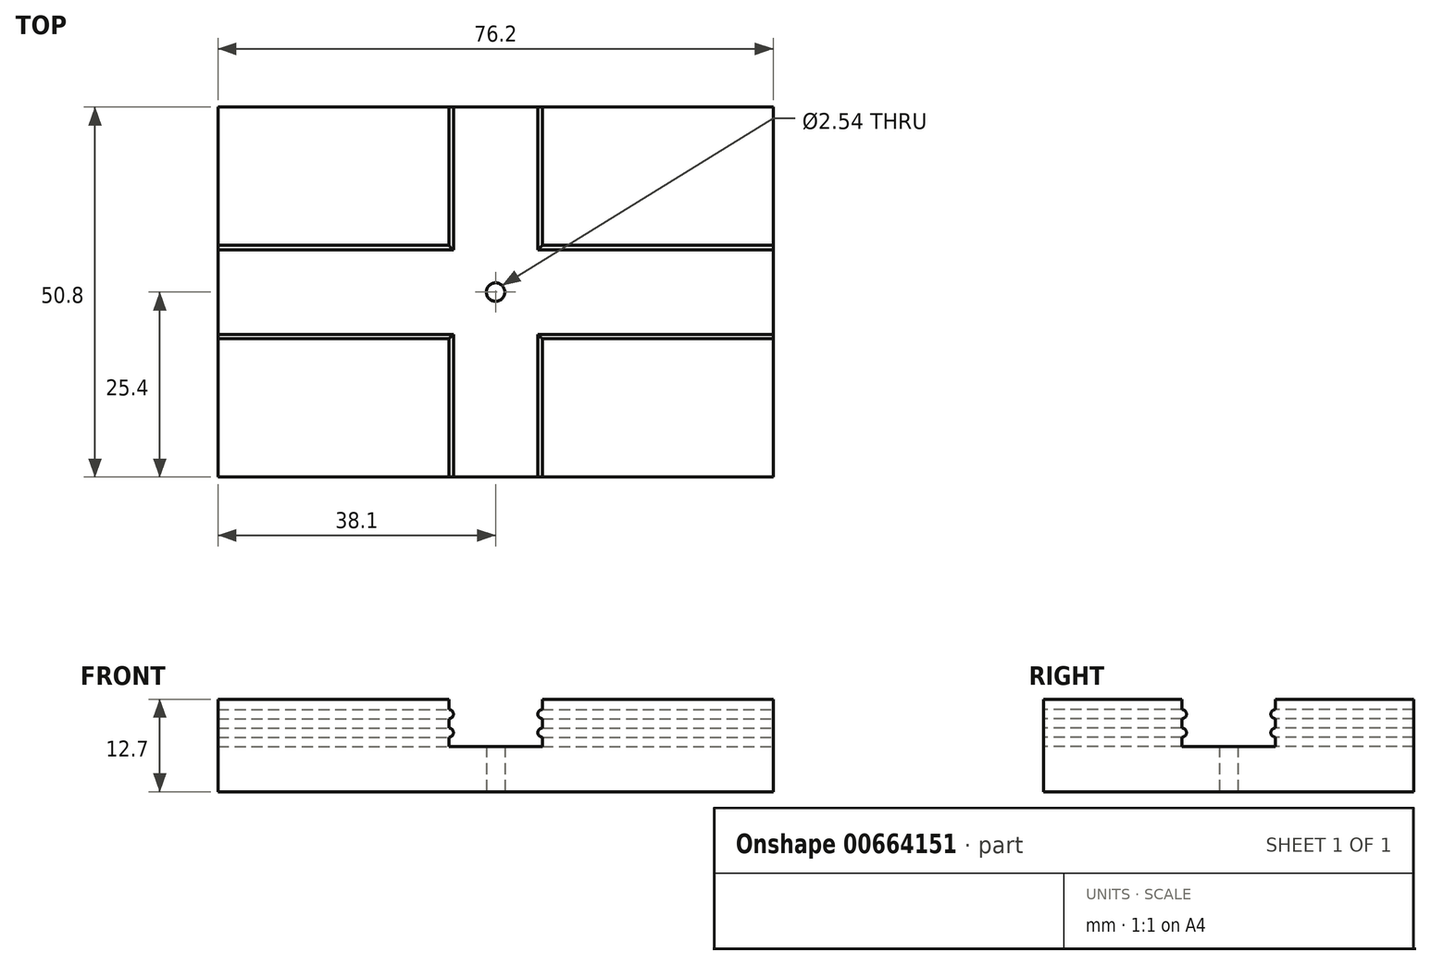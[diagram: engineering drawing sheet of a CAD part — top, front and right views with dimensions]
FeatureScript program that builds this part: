
annotation { "Feature Type Name" : "Feature", "Feature Type Description" : "" }
export const myFeature = defineFeature(function(context is Context, id is Id, definition is map)
    precondition{}
    {
        {
            var Q0;
            Q0=qCreatedBy(makeId("Top.planeOp"),FACE);
            var sketch = newSketch(context, id + "F0", { "sketchPlane" : qUnion([Q0])});
            skLineSegment(sketch, "E0.bottom", {"start": v(-38.1, -25.4) * mm, "end": v(38.1, -25.4) * mm});
            skLineSegment(sketch, "E0.top", {"start": v(-38.1, 25.4) * mm, "end": v(38.1, 25.4) * mm});
            skLineSegment(sketch, "E0.left", {"start": v(-38.1, -25.4) * mm, "end": v(-38.1, 25.4) * mm});
            skLineSegment(sketch, "E0.right", {"start": v(38.1, -25.4) * mm, "end": v(38.1, 25.4) * mm});
            skPoint(sketch, "E0.middle", {"position": v(0, 0) * mm});
            skSolve(sketch);
        }
        {
            var Q0;
            Q0=makeQuery(id+"F0.imprint","IMPRINT",FACE,{"disambiguationData":[TD([[makeQuery(id+"F0.imprint","IMPRINT",EDGE,{"derivedFrom":sQuery(id+"F0.wireOp",EDGE,"E0.bottom")}),1.0]])]});
            extrude(context, id + "F1", {"entities" : qUnion([Q0]), "depth" : 12.7 * mm, "offsetDistance" : 25.4 * mm});
        }
        {
            var Q0;
            Q0=makeQuery(id+"F1.opExtrude","SWEPT_FACE",FACE,{"disambiguationData":[OSD([sQuery(id+"F0.wireOp",EDGE,"E0.bottom")])]});
            var sketch = newSketch(context, id + "F2", { "sketchPlane" : qUnion([Q0])});
            skLineSegment(sketch, "E1.bottom", {"start": v(-6.41, 12.7) * mm, "end": v(6.41, 12.7) * mm});
            skLineSegment(sketch, "E1.top", {"start": v(-6.41, 6.22) * mm, "end": v(6.41, 6.22) * mm});
            skLineSegment(sketch, "E1.left", {"start": v(-6.41, 12.7) * mm, "end": v(-6.41, 6.22) * mm});
            skLineSegment(sketch, "E1.right", {"start": v(6.41, 12.7) * mm, "end": v(6.41, 6.22) * mm});
            skArc(sketch, "E2", {"start": v(-6.41, 11.28) * mm, "mid": v(-5.8, 10.66) * mm, "end": v(-6.41, 10.03) * mm});
            skArc(sketch, "E3", {"start": v(-6.41, 8.74) * mm, "mid": v(-5.8, 8.12) * mm, "end": v(-6.41, 7.5) * mm});
            skArc(sketch, "E4.MirrorCS", {"start": v(6.41, 11.28) * mm, "mid": v(5.8, 10.66) * mm, "end": v(6.41, 10.03) * mm});
            skArc(sketch, "E5.MirrorCS", {"start": v(6.41, 8.74) * mm, "mid": v(5.8, 8.12) * mm, "end": v(6.41, 7.5) * mm});
            skSolve(sketch);
        }
        {
            var Q0;
            {var subQ3=sQuery(id+"F2.wireOp",EDGE,"E1.bottom");Q0=makeQuery(id+"F2.imprint","IMPRINT",FACE,{"disambiguationData":[TD([[makeQuery(id+"F2.imprint","IMPRINT",EDGE,{"derivedFrom":subQ3}),-1.0]])]});}
            var Q1;
            Q1 = qSketchRegion(id + "F4", true);
            extrude(context, id + "F3", {"entities" : qUnion([Q0, Q1]), "operationType" : NewBodyOperationType.REMOVE, "endBound" : BoundingType.THROUGH_ALL, "oppositeDirection" : true, "depth" : 25.4 * mm, "offsetDistance" : 25.4 * mm});
        }
        {
            var Q0;
            Q0=makeQuery(id+"F1.opExtrude","SWEPT_FACE",FACE,{"disambiguationData":[OSD([sQuery(id+"F0.wireOp",EDGE,"E0.right")])]});
            var sketch = newSketch(context, id + "F4", { "sketchPlane" : qUnion([Q0])});
            skLineSegment(sketch, "E6.bottom", {"start": v(-6.41, 12.7) * mm, "end": v(6.41, 12.7) * mm});
            skLineSegment(sketch, "E6.top", {"start": v(-6.41, 6.22) * mm, "end": v(6.41, 6.22) * mm});
            skLineSegment(sketch, "E6.left", {"start": v(-6.41, 12.7) * mm, "end": v(-6.41, 6.22) * mm});
            skLineSegment(sketch, "E6.right", {"start": v(6.41, 12.7) * mm, "end": v(6.41, 6.22) * mm});
            skArc(sketch, "E7", {"start": v(-6.41, 11.28) * mm, "mid": v(-5.8, 10.66) * mm, "end": v(-6.41, 10.03) * mm});
            skArc(sketch, "E8", {"start": v(-6.41, 8.74) * mm, "mid": v(-5.8, 8.12) * mm, "end": v(-6.41, 7.5) * mm});
            skArc(sketch, "E9.MirrorCS", {"start": v(6.41, 8.74) * mm, "mid": v(5.8, 8.12) * mm, "end": v(6.41, 7.5) * mm});
            skArc(sketch, "E10.MirrorCS", {"start": v(6.41, 11.28) * mm, "mid": v(5.8, 10.66) * mm, "end": v(6.41, 10.03) * mm});
            skSolve(sketch);
        }
        {
            var Q0;
            {var subQ3=sQuery(id+"F4.wireOp",EDGE,"E6.bottom");Q0=makeQuery(id+"F4.imprint","IMPRINT",FACE,{"disambiguationData":[TD([[makeQuery(id+"F4.imprint","IMPRINT",EDGE,{"derivedFrom":subQ3}),-1.0]])]});}
            extrude(context, id + "F5", {"entities" : qUnion([Q0]), "operationType" : NewBodyOperationType.REMOVE, "endBound" : BoundingType.THROUGH_ALL, "oppositeDirection" : true, "depth" : 25.4 * mm, "offsetDistance" : 25.4 * mm});
        }
        {
            var Q0;
            Q0=qCreatedBy(makeId("Top.planeOp"),FACE);
            var sketch = newSketch(context, id + "F6", { "sketchPlane" : qUnion([Q0])});
            skCircle(sketch, "E11", {"center": v(0, 0) * mm, "radius": 1.27 * mm});
            skSolve(sketch);
        }
        {
            var Q0;
            Q0=makeQuery(id+"F6.imprint","IMPRINT",FACE,{"disambiguationData":[TD([[makeQuery(id+"F6.imprint","IMPRINT",EDGE,{"derivedFrom":sQuery(id+"F6.wireOp",EDGE,"E11")}),1.0]])]});
            extrude(context, id + "F7", {"entities" : qUnion([Q0]), "operationType" : NewBodyOperationType.REMOVE, "endBound" : BoundingType.THROUGH_ALL, "depth" : 25.4 * mm, "offsetDistance" : 25.4 * mm});
        }
    });
